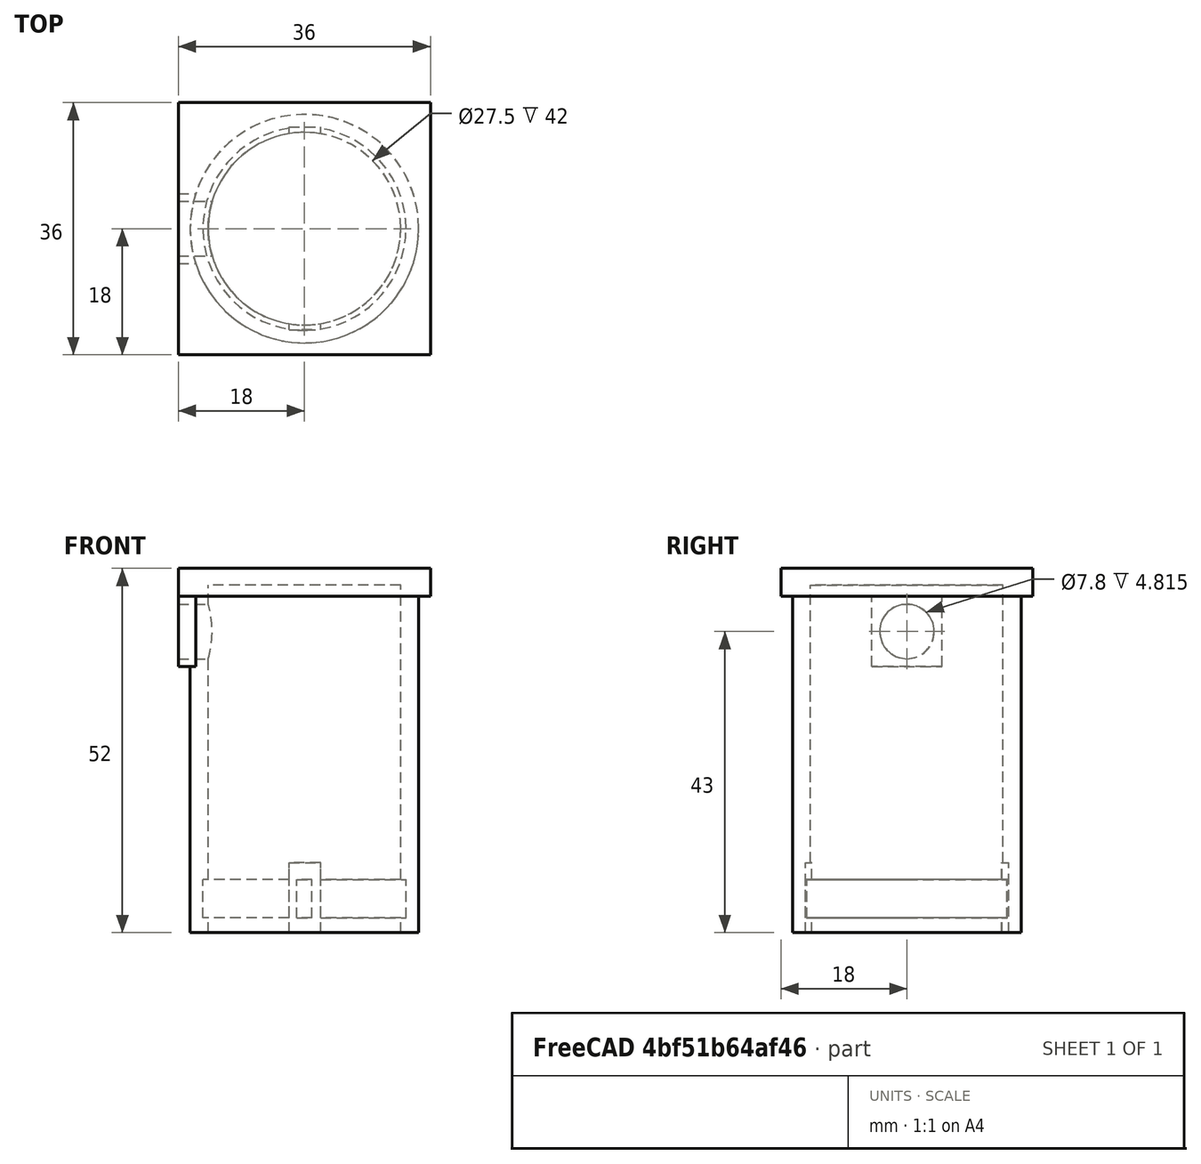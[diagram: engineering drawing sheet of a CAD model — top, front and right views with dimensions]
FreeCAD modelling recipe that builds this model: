
FCSTD DOCUMENT  (FreeCAD 0.18.4R)
Label: car-cigarette-lighter-adapter
License: All rights reserved
LicenseURL: http://en.wikipedia.org/wiki/All_rights_reserved
objects: Part::Cylinder×4, Part::Cut×4, Part::Box×3, Part::MultiFuse×1
note: 12 computed .brp shape members not serialized (recipe doc carries the construction recipe); baked Part::Feature solids carry a one-line shape summary decoded from their .brp

FEATURE [Part::Cylinder] Cylinder
  Angle = 360
  AttacherType = Attacher::AttachEngine3D
  Height = 49.6
  Radius = 13.75
FEATURE [Part::Box] Box  label="Cube"
  AttacherType = Attacher::AttachEngine3D
  Height = 4
  Length = 36
  Placement = pos=(-18,-18,48) rot=(0,0,1;0rad)
  Width = 36
FEATURE [Part::Box] Box001  label="Cube001"
  AttacherType = Attacher::AttachEngine3D
  Height = 10
  Length = 10
  Placement = pos=(-18,-5,38) rot=(0,0,1;0rad)
  Width = 10
FEATURE [Part::Cylinder] Cylinder001
  Angle = 360
  AttacherType = Attacher::AttachEngine3D
  Height = 52
  Radius = 16.32
FEATURE [Part::MultiFuse] Fusion
  Shapes = -> [Cylinder001,Box,Box001]
FEATURE [Part::Cut] Cut
  Base = -> Fusion
  Tool = -> Cylinder
FEATURE [Part::Cylinder] Cylinder002
  Angle = 360
  AttacherType = Attacher::AttachEngine3D
  Height = 10
  Placement = pos=(-20,0,43) rot=(0,1,0;1.5708rad)
  Radius = 3.9
FEATURE [Part::Cut] Cut001
  Base = -> Cut
  Tool = -> Cylinder002
FEATURE [Part::Cylinder] Cylinder003
  Angle = 360
  AttacherType = Attacher::AttachEngine3D
  Height = 5.5
  Placement = pos=(0,0,2.1) rot=(0,0,1;0rad)
  Radius = 14.5
FEATURE [Part::Cut] Cut002
  Base = -> Cut001
  Tool = -> Cylinder003
FEATURE [Part::Box] Box002  label="Cube002"
  AttacherType = Attacher::AttachEngine3D
  Height = 10
  Length = 4.5
  Placement = pos=(-2.2,-14.46,0) rot=(0,0,1;0rad)
  Width = 29
FEATURE [Part::Cut] Cut003
  Base = -> Cut002
  Tool = -> Box002
